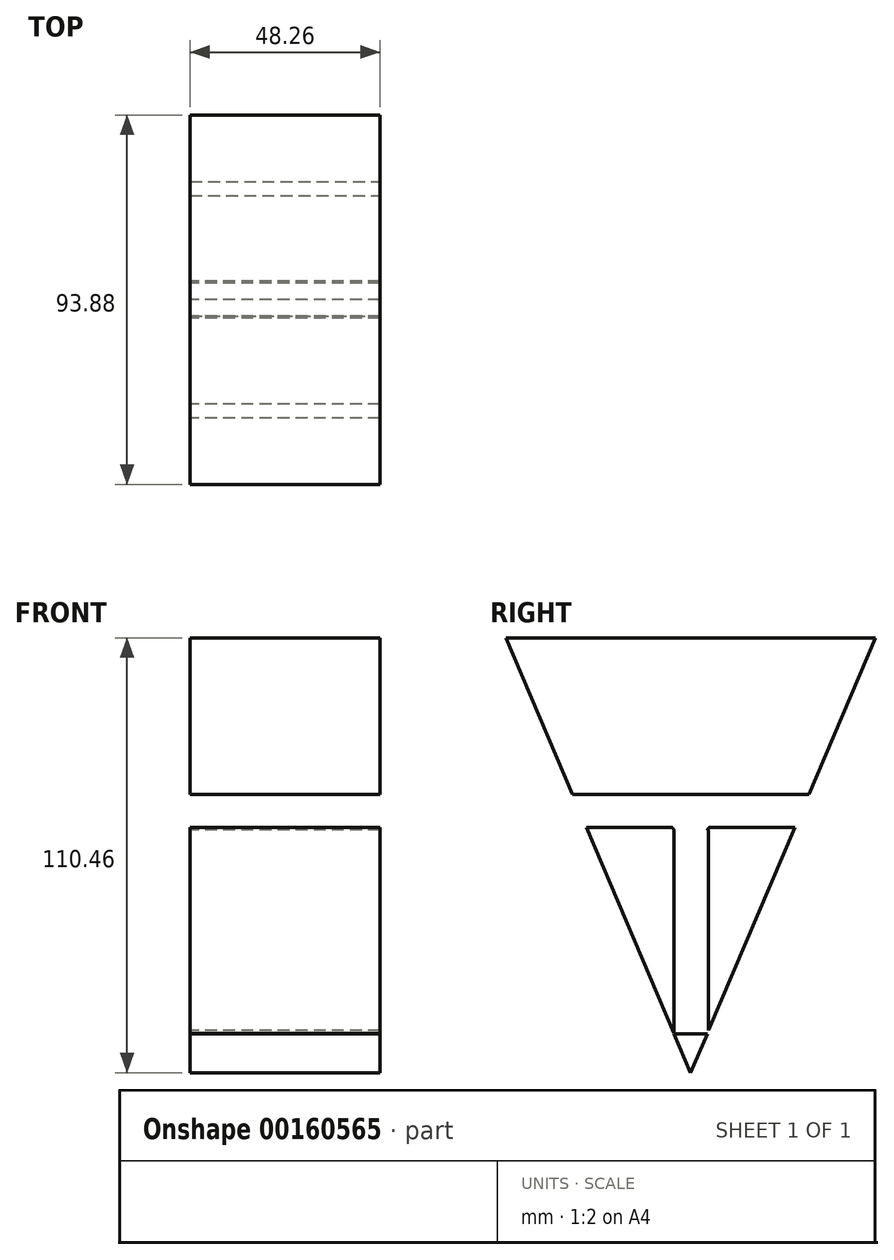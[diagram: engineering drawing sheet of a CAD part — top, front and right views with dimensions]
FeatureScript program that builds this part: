
annotation { "Feature Type Name" : "Feature", "Feature Type Description" : "" }
export const myFeature = defineFeature(function(context is Context, id is Id, definition is map)
    precondition{}
    {
        {
            var Q0;
            Q0=qCreatedBy(makeId("Right.planeOp"),FACE);
            var sketch = newSketch(context, id + "F0", { "sketchPlane" : qUnion([Q0])});
            skLineSegment(sketch, "E0", {"start": v(-46.94, 45.26) * mm, "end": v(0, -65.2) * mm});
            skLineSegment(sketch, "E1", {"start": v(-46.94, 45.26) * mm, "end": v(46.94, 45.26) * mm});
            skLineSegment(sketch, "E2", {"start": v(0, -65.2) * mm, "end": v(46.94, 45.26) * mm});
            skSolve(sketch);
        }
        {
            var Q0;
            Q0 = qSketchRegion(id + "F0", true);
            extrude(context, id + "F1", {"entities" : qUnion([Q0]), "endBound" : BoundingType.SYMMETRIC, "depth" : 48.26 * mm});
        }
        {
            var Q0;
            Q0=makeQuery(id+"F1.opExtrude","CAP_FACE",FACE,{"disambiguationData":[OSD([sQuery(id+"F0.wireOp",EDGE,"E0"),sQuery(id+"F0.wireOp",EDGE,"E1"),sQuery(id+"F0.wireOp",EDGE,"E2")])],"isStart":false});
            var sketch = newSketch(context, id + "F2", { "sketchPlane" : qUnion([Q0])});
            skCircle(sketch, "E3", {"center": v(0, 0) * mm, "radius": 5.49 * mm});
            skLineSegment(sketch, "E4.bottom", {"start": v(-4.27, -3.5) * mm, "end": v(4.57, -3.5) * mm});
            skLineSegment(sketch, "E4.top", {"start": v(-4.27, -55.32) * mm, "end": v(4.57, -55.32) * mm});
            skLineSegment(sketch, "E4.left", {"start": v(-4.27, -3.5) * mm, "end": v(-4.27, -55.32) * mm});
            skLineSegment(sketch, "E4.right", {"start": v(4.57, -3.5) * mm, "end": v(4.57, -55.32) * mm});
            skLineSegment(sketch, "E5.bottom", {"start": v(0, 5.49) * mm, "end": v(5.49, 5.49) * mm});
            skLineSegment(sketch, "E5.top", {"start": v(0, 0) * mm, "end": v(5.49, 0) * mm});
            skLineSegment(sketch, "E5.left", {"start": v(0, 5.49) * mm, "end": v(0, 0) * mm});
            skLineSegment(sketch, "E5.right", {"start": v(5.49, 5.49) * mm, "end": v(5.49, 0) * mm});
            skLineSegment(sketch, "E6.bottom", {"start": v(5.49, 5.49) * mm, "end": v(31.7, 5.49) * mm});
            skLineSegment(sketch, "E6.top", {"start": v(5.49, -2.9) * mm, "end": v(31.7, -2.9) * mm});
            skLineSegment(sketch, "E6.left", {"start": v(5.49, 5.49) * mm, "end": v(5.49, -2.9) * mm});
            skLineSegment(sketch, "E6.right", {"start": v(31.7, 5.49) * mm, "end": v(31.7, -2.9) * mm});
            skLineSegment(sketch, "E7.bottom", {"start": v(32.61, -2.9) * mm, "end": v(-30.04, -2.9) * mm});
            skLineSegment(sketch, "E7.top", {"start": v(32.61, 5.49) * mm, "end": v(-30.04, 5.49) * mm});
            skLineSegment(sketch, "E7.left", {"start": v(32.61, -2.9) * mm, "end": v(32.61, 5.49) * mm});
            skLineSegment(sketch, "E7.right", {"start": v(-30.04, -2.9) * mm, "end": v(-30.04, 5.49) * mm});
            skSolve(sketch);
        }
        {
            var Q0;
            Q0 = qSketchRegion(id + "F2", true);
            extrude(context, id + "F3", {"entities" : qUnion([Q0]), "operationType" : NewBodyOperationType.REMOVE, "endBound" : BoundingType.SYMMETRIC, "depth" : 1397 * mm});
        }
    });
